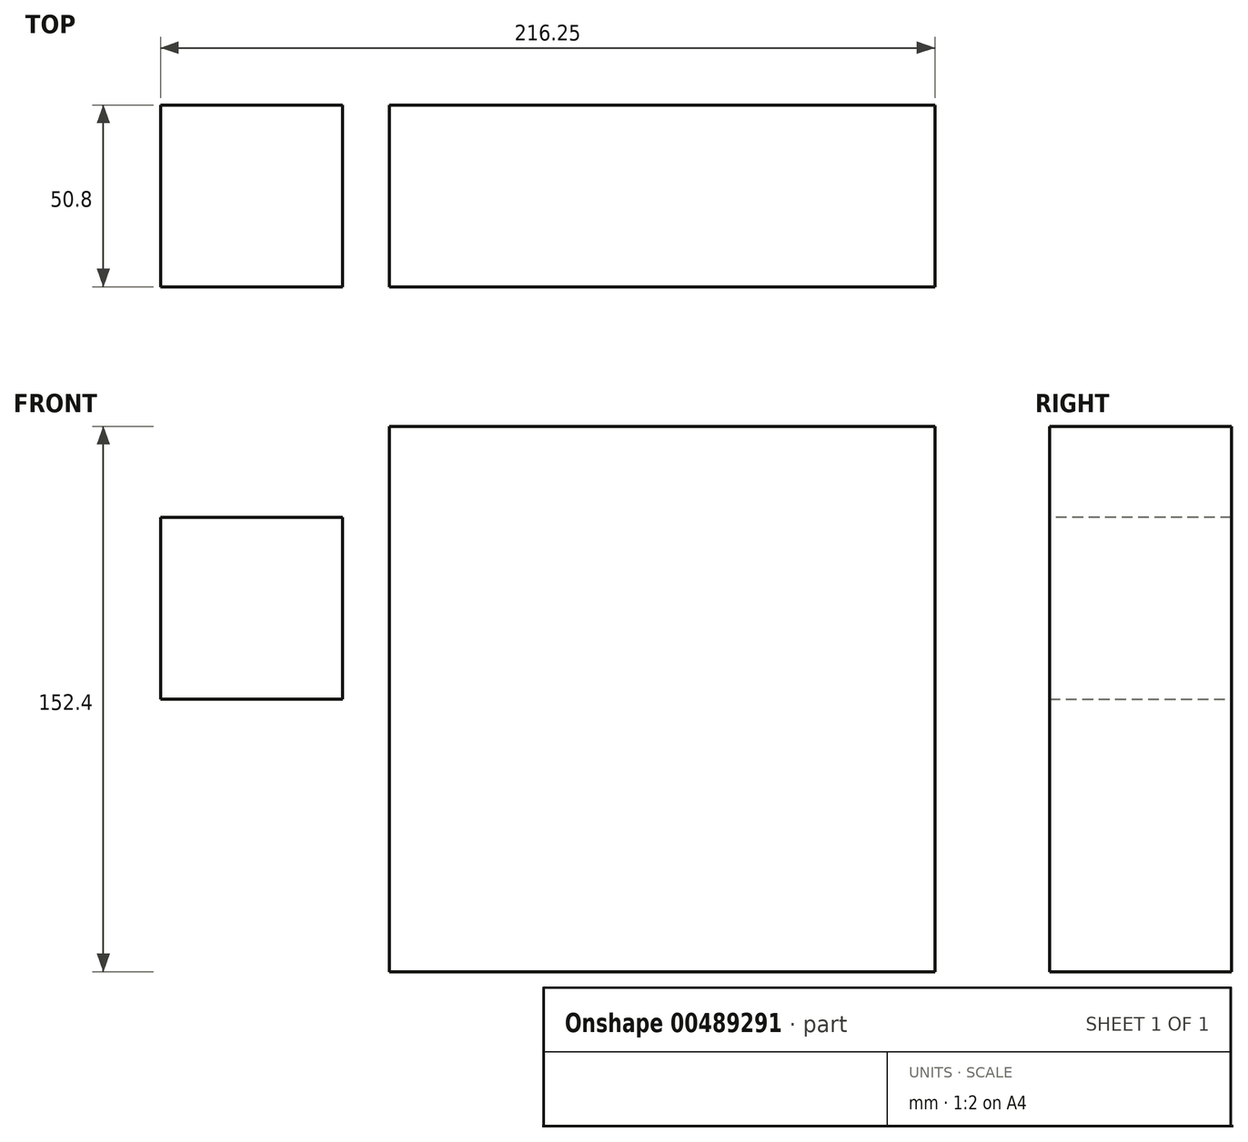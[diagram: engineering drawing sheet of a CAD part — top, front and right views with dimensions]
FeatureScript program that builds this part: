
annotation { "Feature Type Name" : "Feature", "Feature Type Description" : "" }
export const myFeature = defineFeature(function(context is Context, id is Id, definition is map)
    precondition{}
    {
        {
            var Q0;
            Q0=qCreatedBy(makeId("Front.planeOp"),FACE);
            var sketch = newSketch(context, id + "F0", { "sketchPlane" : qUnion([Q0])});
            skLineSegment(sketch, "E0.bottom", {"start": v(-76.2, -76.2) * mm, "end": v(76.2, -76.2) * mm});
            skLineSegment(sketch, "E0.top", {"start": v(-76.2, 76.2) * mm, "end": v(76.2, 76.2) * mm});
            skLineSegment(sketch, "E0.left", {"start": v(-76.2, -76.2) * mm, "end": v(-76.2, 76.2) * mm});
            skLineSegment(sketch, "E0.right", {"start": v(76.2, -76.2) * mm, "end": v(76.2, 76.2) * mm});
            skPoint(sketch, "E0.middle", {"position": v(0, 0) * mm});
            skLineSegment(sketch, "E1.bottom", {"start": v(-140.05, 50.8) * mm, "end": v(-89.25, 50.8) * mm});
            skLineSegment(sketch, "E1.top", {"start": v(-140.05, 0) * mm, "end": v(-89.25, 0) * mm});
            skLineSegment(sketch, "E1.left", {"start": v(-140.05, 50.8) * mm, "end": v(-140.05, 0) * mm});
            skLineSegment(sketch, "E1.right", {"start": v(-89.25, 50.8) * mm, "end": v(-89.25, 0) * mm});
            skSolve(sketch);
        }
        {
            var Q0;
            Q0 = qSketchRegion(id + "F0", true);
            extrude(context, id + "F1", {"entities" : qUnion([Q0]), "depth" : 50.8 * mm, "hasDraft" : true, "draftAngle" : 0 * degree});
        }
    });
